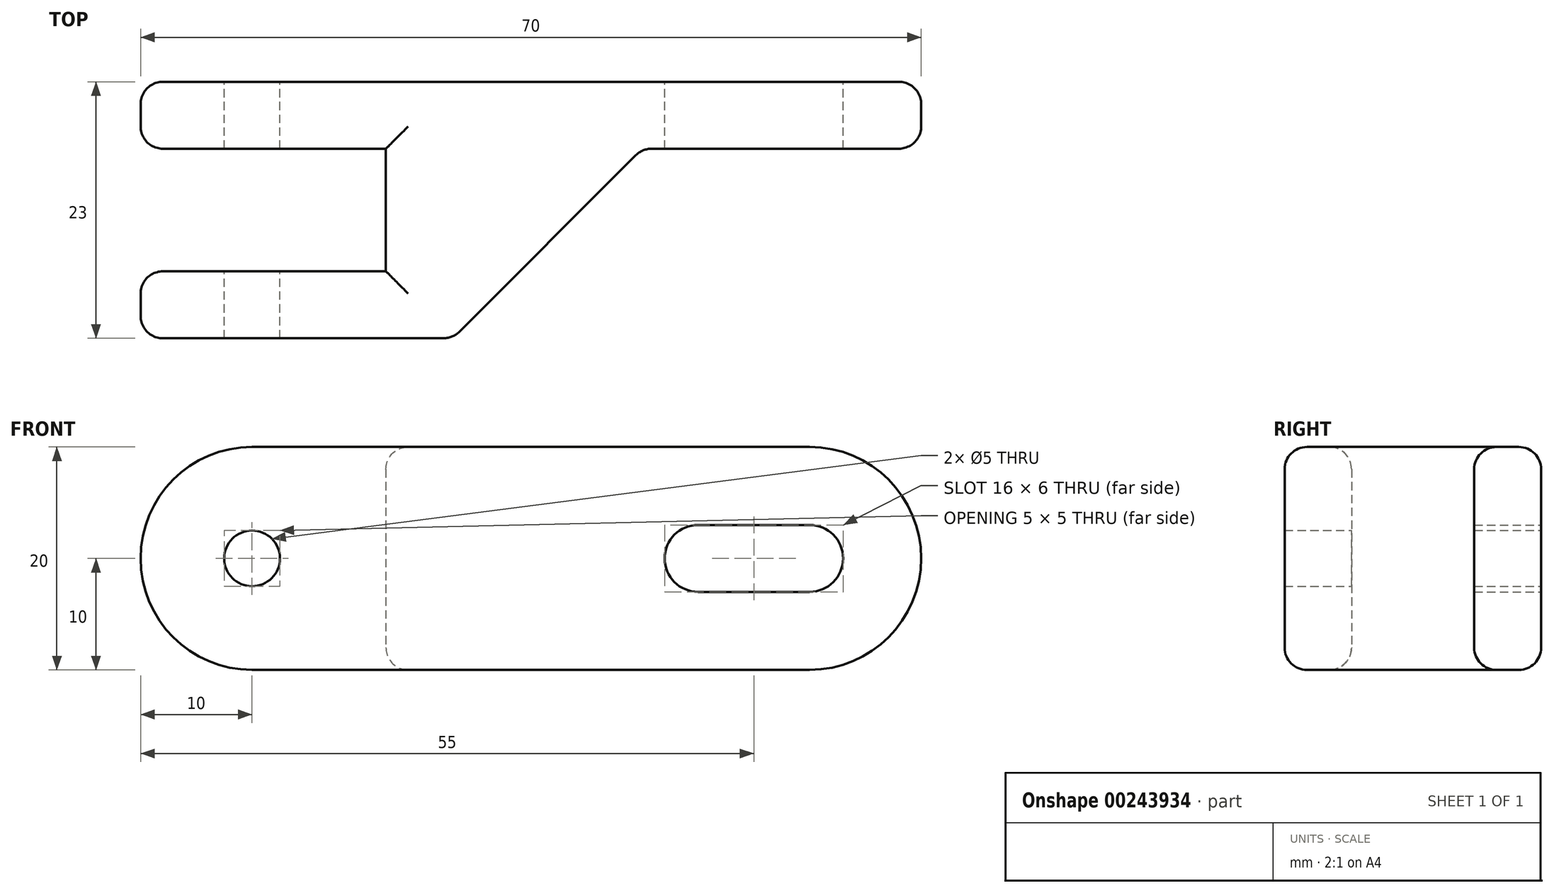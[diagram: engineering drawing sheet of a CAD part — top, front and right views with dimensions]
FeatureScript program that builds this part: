
annotation { "Feature Type Name" : "Feature", "Feature Type Description" : "" }
export const myFeature = defineFeature(function(context is Context, id is Id, definition is map)
    precondition{}
    {
        {
            var Q0;
            Q0=qCreatedBy(makeId("Top.planeOp"),FACE);
            var sketch = newSketch(context, id + "F0", { "sketchPlane" : qUnion([Q0])});
            skLineSegment(sketch, "E0", {"start": v(0, 0) * mm, "end": v(70, 0) * mm});
            skLineSegment(sketch, "E1", {"start": v(0, 0) * mm, "end": v(0, -6) * mm});
            skLineSegment(sketch, "E2", {"start": v(0, -6) * mm, "end": v(22, -6) * mm});
            skLineSegment(sketch, "E3", {"start": v(22, -6) * mm, "end": v(22, -17) * mm});
            skLineSegment(sketch, "E4", {"start": v(22, -17) * mm, "end": v(0, -17) * mm});
            skLineSegment(sketch, "E5", {"start": v(0, -17) * mm, "end": v(0, -23) * mm});
            skLineSegment(sketch, "E6", {"start": v(0, -23) * mm, "end": v(28, -23) * mm});
            skLineSegment(sketch, "E7", {"start": v(70, 0) * mm, "end": v(70, -6) * mm});
            skLineSegment(sketch, "E8", {"start": v(70, -6) * mm, "end": v(45, -6) * mm});
            skLineSegment(sketch, "E9", {"start": v(45, -6) * mm, "end": v(28, -23) * mm});
            skSolve(sketch);
        }
        {
            var Q0;
            Q0=makeQuery(id+"F0.imprint","IMPRINT",FACE,{"disambiguationData":[TD([[makeQuery(id+"F0.imprint","IMPRINT",EDGE,{"derivedFrom":sQuery(id+"F0.wireOp",EDGE,"E0")}),-1.0]])]});
            extrude(context, id + "F1", {"entities" : qUnion([Q0]), "depth" : 20 * mm});
        }
        {
            var Q0;
            Q0=qCreatedBy(makeId("Front.planeOp"),FACE);
            var sketch = newSketch(context, id + "F2", { "sketchPlane" : qUnion([Q0])});
            skLineSegment(sketch, "E10", {"start": v(0, 0) * mm, "end": v(10, 0) * mm, "construction": true});
            skLineSegment(sketch, "E11", {"start": v(10, 0) * mm, "end": v(10, 7.5) * mm, "construction": true});
            skLineSegment(sketch, "E12", {"start": v(10, 0) * mm, "end": v(60, 0) * mm, "construction": true});
            skLineSegment(sketch, "E13", {"start": v(60, 0) * mm, "end": v(60, 10) * mm, "construction": true});
            skLineSegment(sketch, "E14", {"start": v(60, 10) * mm, "end": v(50, 10) * mm, "construction": true});
            skArc(sketch, "E15", {"start": v(60, 7) * mm, "mid": v(63, 10) * mm, "end": v(60, 13) * mm});
            skArc(sketch, "E16", {"start": v(50, 13) * mm, "mid": v(47, 10) * mm, "end": v(50, 7) * mm});
            skCircle(sketch, "E17", {"center": v(10, 10) * mm, "radius": 2.5 * mm});
            skArc(sketch, "E18", {"start": v(10, 20) * mm, "mid": v(0, 10) * mm, "end": v(10, 0) * mm});
            skLineSegment(sketch, "E19", {"start": v(60, 20) * mm, "end": v(72, 20) * mm});
            skLineSegment(sketch, "E20", {"start": v(72, 20) * mm, "end": v(72, 0) * mm});
            skLineSegment(sketch, "E21", {"start": v(72, 0) * mm, "end": v(60, 0) * mm});
            skLineSegment(sketch, "E22", {"start": v(10, 20) * mm, "end": v(-2, 20) * mm});
            skLineSegment(sketch, "E23", {"start": v(-2, 20) * mm, "end": v(-2, 0) * mm});
            skLineSegment(sketch, "E24", {"start": v(-2, 0) * mm, "end": v(10, 0) * mm});
            skLineSegment(sketch, "E25.0", {"start": v(60, 13) * mm, "end": v(50, 13) * mm});
            skLineSegment(sketch, "E26.0", {"start": v(60, 7) * mm, "end": v(50, 7) * mm});
            skArc(sketch, "E27.trimOffspring", {"start": v(60, 0) * mm, "mid": v(70, 10) * mm, "end": v(60, 20) * mm});
            skSolve(sketch);
        }
        {
            var Q0;
            Q0=makeQuery(id+"F2.imprint","IMPRINT",FACE,{"disambiguationData":[TD([[makeQuery(id+"F2.imprint","IMPRINT",EDGE,{"derivedFrom":sQuery(id+"F2.wireOp",EDGE,"E19")}),-1.0]])]});
            var Q1;
            Q1=makeQuery(id+"F2.imprint","IMPRINT",FACE,{"disambiguationData":[TD([[makeQuery(id+"F2.imprint","IMPRINT",EDGE,{"derivedFrom":sQuery(id+"F2.wireOp",EDGE,"E18")}),-1.0]])]});
            var Q2;
            Q2=makeQuery(id+"F2.imprint","IMPRINT",FACE,{"disambiguationData":[TD([[makeQuery(id+"F2.imprint","IMPRINT",EDGE,{"derivedFrom":sQuery(id+"F2.wireOp",EDGE,"E15")}),1.0]])]});
            var Q3;
            Q3=makeQuery(id+"F2.imprint","IMPRINT",FACE,{"disambiguationData":[TD([[makeQuery(id+"F2.imprint","IMPRINT",EDGE,{"derivedFrom":sQuery(id+"F2.wireOp",EDGE,"E17")}),1.0]])]});
            extrude(context, id + "F3", {"entities" : qUnion([Q0, Q1, Q2, Q3]), "operationType" : NewBodyOperationType.REMOVE, "depth" : 25 * mm});
        }
        {
            var Q0;
            Q0=makeQuery(id+"F1.opExtrude","CAP_FACE",FACE,{"disambiguationData":[OSD([sQuery(id+"F0.wireOp",EDGE,"E0"),sQuery(id+"F0.wireOp",EDGE,"E1"),sQuery(id+"F0.wireOp",EDGE,"E2"),sQuery(id+"F0.wireOp",EDGE,"E3"),sQuery(id+"F0.wireOp",EDGE,"E4"),sQuery(id+"F0.wireOp",EDGE,"E5"),sQuery(id+"F0.wireOp",EDGE,"E6"),sQuery(id+"F0.wireOp",EDGE,"E7"),sQuery(id+"F0.wireOp",EDGE,"E8"),sQuery(id+"F0.wireOp",EDGE,"E9")])],"isStart":false});
            var Q1;
            Q1=makeQuery(id+"F1.opExtrude","CAP_EDGE",EDGE,{"disambiguationData":[OSD([sQuery(id+"F0.wireOp",EDGE,"E9")])],"isStart":true});
            var Q2;
            Q2=makeQuery(id+"F1.opExtrude","SWEPT_EDGE",EDGE,{"disambiguationData":[OSD([sQuery(id+"F0.wireOp",EDGE,"E8"),sQuery(id+"F0.wireOp",EDGE,"E9")])]});
            var Q3;
            Q3=makeQuery(id+"F1.opExtrude","SWEPT_EDGE",EDGE,{"disambiguationData":[OSD([sQuery(id+"F0.wireOp",EDGE,"E6"),sQuery(id+"F0.wireOp",EDGE,"E9")])]});
            var Q4;
            Q4=makeQuery(id+"F1.opExtrude","CAP_EDGE",EDGE,{"disambiguationData":[OSD([sQuery(id+"F0.wireOp",EDGE,"E3")])],"isStart":true});
            fillet(context, id + "F4", {"entities" : qUnion([Q0, Q1, Q2, Q3, Q4]), "radius" : 2 * mm, "tangentPropagation" : true, "allowEdgeOverflow" : false});
        }
    });
